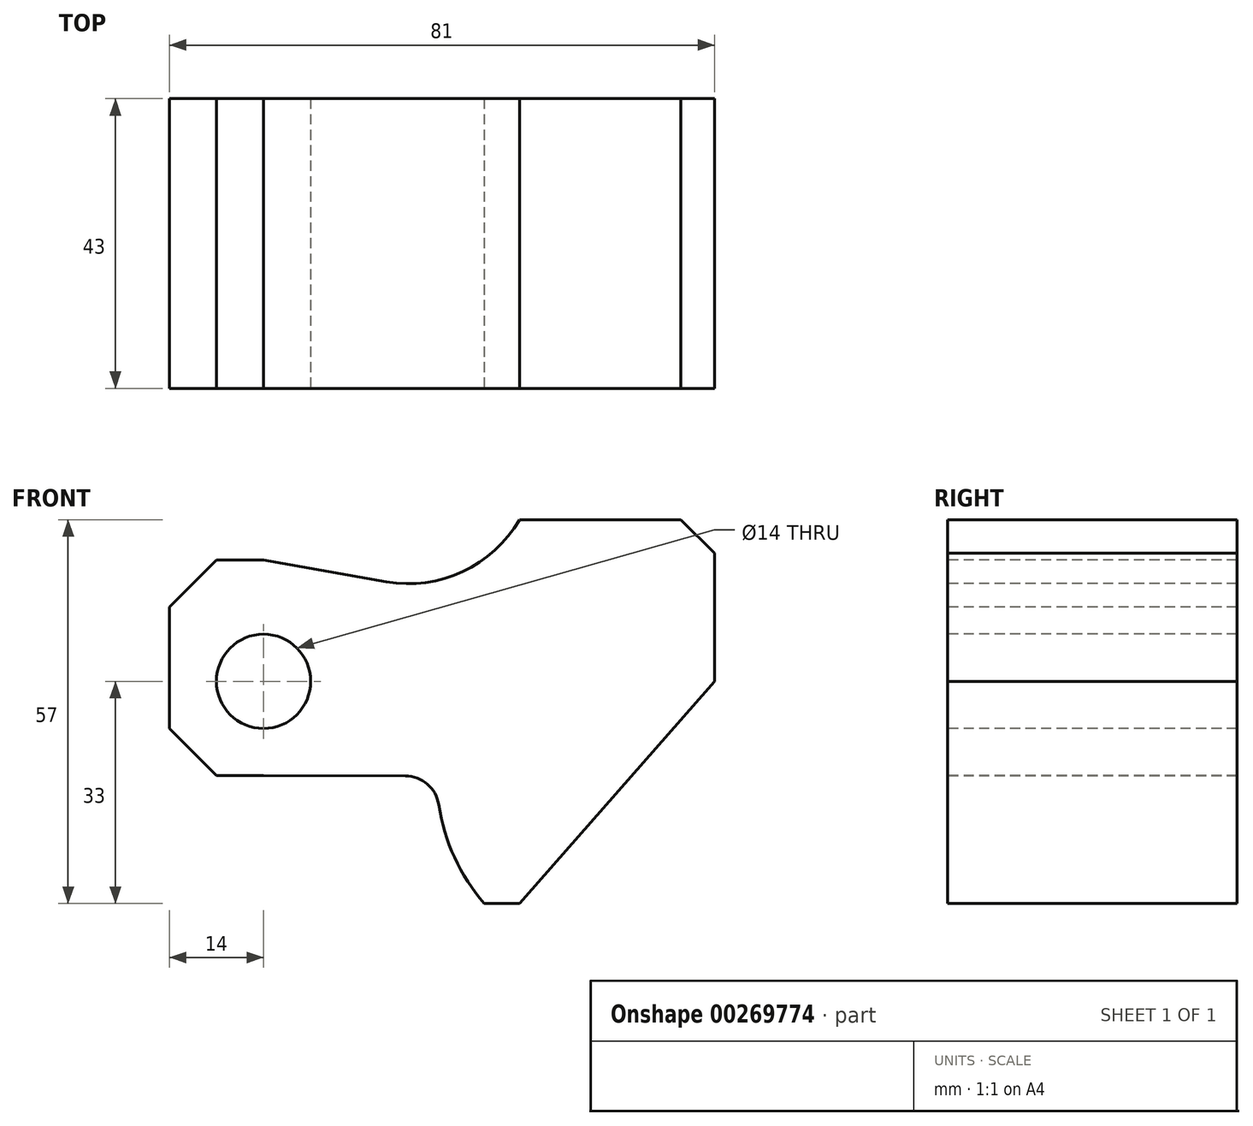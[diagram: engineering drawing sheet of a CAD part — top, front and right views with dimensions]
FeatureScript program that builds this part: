
annotation { "Feature Type Name" : "Feature", "Feature Type Description" : "" }
export const myFeature = defineFeature(function(context is Context, id is Id, definition is map)
    precondition{}
    {
        {
            var Q0;
            Q0=qCreatedBy(makeId("Front.planeOp"),FACE);
            var sketch = newSketch(context, id + "F0", { "sketchPlane" : qUnion([Q0])});
            skCircle(sketch, "E0", {"center": v(0, 0) * mm, "radius": 7 * mm});
            skLineSegment(sketch, "E1", {"start": v(-14, -7) * mm, "end": v(-14, 11) * mm});
            skLineSegment(sketch, "E2", {"start": v(-14, -7) * mm, "end": v(-7, -14) * mm});
            skLineSegment(sketch, "E3", {"start": v(0, -14) * mm, "end": v(-7, -14) * mm});
            skPoint(sketch, "E4.endSnap0", {"position": v(-14, 2) * mm});
            skLineSegment(sketch, "E5.MirrorCS", {"start": v(-14, -21) * mm, "end": v(-7, -14) * mm});
            skLineSegment(sketch, "E6", {"start": v(-7, 18) * mm, "end": v(0, 18) * mm});
            skLineSegment(sketch, "E7", {"start": v(-7, 18) * mm, "end": v(-14, 11) * mm});
            skLineSegment(sketch, "E8", {"start": v(0, 18) * mm, "end": v(18.24, 14.78) * mm});
            skLineSegment(sketch, "E9", {"start": v(18.24, 14.78) * mm, "end": v(18.24, 14.78) * mm});
            skLineSegment(sketch, "E10", {"start": v(67, 0) * mm, "end": v(67, 19) * mm});
            skLineSegment(sketch, "E11", {"start": v(67, 19) * mm, "end": v(62, 24) * mm});
            skLineSegment(sketch, "E12", {"start": v(67, 19) * mm, "end": v(67, 24) * mm});
            skLineSegment(sketch, "E13", {"start": v(62, 24) * mm, "end": v(38, 24) * mm});
            skArc(sketch, "E14", {"start": v(18.24, 14.78) * mm, "mid": v(29.57, 16.28) * mm, "end": v(38, 24) * mm});
            skPoint(sketch, "E15", {"position": v(38, -33) * mm});
            skPoint(sketch, "E16", {"position": v(67, 0) * mm});
            skLineSegment(sketch, "E17", {"start": v(38, -33) * mm, "end": v(67, 0) * mm});
            skPoint(sketch, "E18", {"position": v(54.7, -14) * mm});
            skArc(sketch, "E19", {"start": v(26.02, -18.31) * mm, "mid": v(28.36, -26.14) * mm, "end": v(32.79, -33) * mm});
            skLineSegment(sketch, "E20", {"start": v(32.79, -33) * mm, "end": v(38, -33) * mm});
            skArc(sketch, "E21", {"start": v(26.02, -18.31) * mm, "mid": v(24.34, -15.27) * mm, "end": v(21.08, -14.06) * mm});
            skLineSegment(sketch, "E22", {"start": v(0, -14) * mm, "end": v(21.08, -14.06) * mm});
            skSolve(sketch);
        }
        {
            var Q0;
            Q0=makeQuery(id+"F0.imprint","IMPRINT",FACE,{"disambiguationData":[TD([[makeQuery(id+"F0.imprint","IMPRINT",EDGE,{"derivedFrom":sQuery(id+"F0.wireOp",EDGE,"E0")}),-1.0]])]});
            extrude(context, id + "F1", {"entities" : qUnion([Q0]), "oppositeDirection" : true, "depth" : 43 * mm});
        }
    });
